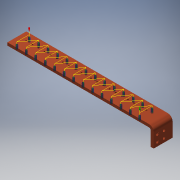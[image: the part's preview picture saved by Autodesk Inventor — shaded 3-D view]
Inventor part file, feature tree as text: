
AUTODESK INVENTOR PART (.ipt)
format: ipt  version: 2016 SP2 (Build 200236200, 236)  size: 428,544 bytes
history: native  units: mm
features: reference x21, sketch x7, hole x3, extrude x1, other x1, pattern_linear x1, projected_geometry x1
ambient origin geometry x8: Origin, YZ Plane, XZ Plane, XY Plane, X Axis, Y Axis, Z Axis, Center Point
bodies: Solid1 (feature_tree)
feature tree (35):
  extrude  "Extrusion1"  Depth=6.0mm
  other  "Bend Part1"
  hole  "Hole2"  [1 undecoded]
  hole  "Hole3"  [1 undecoded]
  pattern_linear  "Rectangular Pattern1"  Count1=14  [1 undecoded]
  hole  "Hole6"  [1 undecoded]
  sketch  "Sketch9"  dims[d25=6.0mm]
  sketch  "Sketch12"  dims[d26=3.242mm d27=6.0mm d28=6.0mm d29=3.2mm d30=90.0deg d31=6.0mm d32=20.594885mm d33=140.0mm d35=20.0mm d51=14.0mm d52=14.0mm d53=15.0mm d54=15.0mm d62=5.3mm d63=6.0mm d64=6.0mm d65=3.2mm d66=90.0deg d67=6.0mm d68=20.594885mm]
  sketch  "Sketch1"  dims[d0=40.0mm d1=6.0mm]
  sketch  "Sketch2"  dims[d2=345.0mm d3=0.0mm d4=315.0mm]
  projected_geometry  "Projected Loop1"
  sketch  "Sketch4"  dims[d5=10.0mm d6=90.0deg]
  reference  "Reference3"
  reference  "Reference4"
  reference  "Reference5"
  reference  "Reference6"
  reference  "Reference7"
  reference  "Reference8"
  reference  "Reference9"
  reference  "Reference10"
  reference  "Reference11"
  reference  "Reference12"
  reference  "Reference13"
  reference  "Reference14"
  reference  "Reference15"
  reference  "Reference16"
  reference  "Reference17"
  reference  "Reference18"
  reference  "Reference19"
  reference  "Reference20"
  reference  "Reference21"
  reference  "Reference22"
  sketch  "Sketch5"  dims[d16=3.2mm d17=6.0mm d18=6.0mm d19=3.2mm d20=90.0deg d21=8.0mm d22=20.594885mm d23=10.0mm]
  reference  "Reference23"
  sketch  "Sketch6"  dims[d24=8.0mm]
note: 4 required parameter values undecoded (feature->parameter linkage not recoverable at this tier; creation-order binding heuristic only, values carry confidence <= 0.55)
